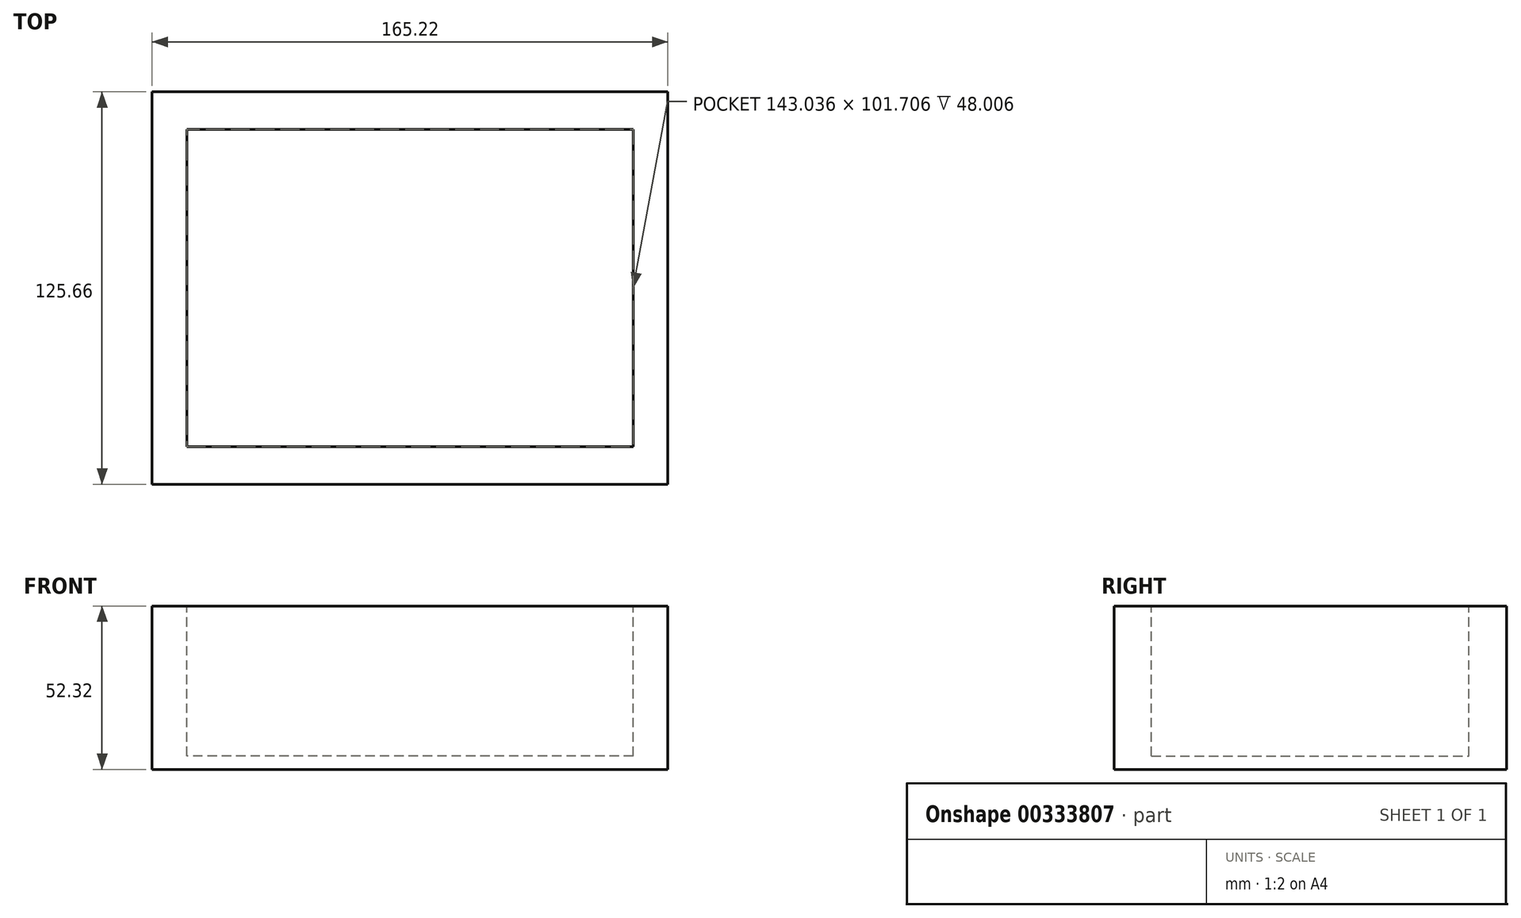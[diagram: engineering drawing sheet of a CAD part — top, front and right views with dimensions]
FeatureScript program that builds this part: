
annotation { "Feature Type Name" : "Feature", "Feature Type Description" : "" }
export const myFeature = defineFeature(function(context is Context, id is Id, definition is map)
    precondition{}
    {
        {
            var Q0;
            Q0=qCreatedBy(makeId("Top.planeOp"),FACE);
            var sketch = newSketch(context, id + "F0", { "sketchPlane" : qUnion([Q0])});
            skLineSegment(sketch, "E0.bottom", {"start": v(82.61, -62.83) * mm, "end": v(-82.61, -62.83) * mm});
            skLineSegment(sketch, "E0.top", {"start": v(82.61, 62.83) * mm, "end": v(-82.61, 62.83) * mm});
            skLineSegment(sketch, "E0.left", {"start": v(82.61, -62.83) * mm, "end": v(82.61, 62.83) * mm});
            skLineSegment(sketch, "E0.right", {"start": v(-82.61, -62.83) * mm, "end": v(-82.61, 62.83) * mm});
            skPoint(sketch, "E0.middle", {"position": v(0, 0) * mm});
            skSolve(sketch);
        }
        {
            var Q0;
            Q0 = qSketchRegion(id + "F0", true);
            extrude(context, id + "F1", {"entities" : qUnion([Q0]), "depth" : 52.32 * mm});
        }
        {
            var Q0;
            Q0=makeQuery(id+"F1.opExtrude","CAP_FACE",FACE,{"disambiguationData":[OSD([sQuery(id+"F0.wireOp",EDGE,"E0.bottom"),sQuery(id+"F0.wireOp",EDGE,"E0.top"),sQuery(id+"F0.wireOp",EDGE,"E0.left"),sQuery(id+"F0.wireOp",EDGE,"E0.right")])],"isStart":false});
            var sketch = newSketch(context, id + "F2", { "sketchPlane" : qUnion([Q0])});
            skLineSegment(sketch, "E1.bottom", {"start": v(71.52, -50.85) * mm, "end": v(-71.52, -50.85) * mm});
            skLineSegment(sketch, "E1.top", {"start": v(71.52, 50.85) * mm, "end": v(-71.52, 50.85) * mm});
            skLineSegment(sketch, "E1.left", {"start": v(71.52, -50.85) * mm, "end": v(71.52, 50.85) * mm});
            skLineSegment(sketch, "E1.right", {"start": v(-71.52, -50.85) * mm, "end": v(-71.52, 50.85) * mm});
            skPoint(sketch, "E1.middle", {"position": v(0, 0) * mm});
            skSolve(sketch);
        }
        {
            var Q0;
            Q0=makeQuery(id+"F2.imprint","IMPRINT",FACE,{"disambiguationData":[TD([[makeQuery(id+"F2.imprint","IMPRINT",EDGE,{"derivedFrom":sQuery(id+"F2.wireOp",EDGE,"E1.bottom")}),-1.0]])]});
            extrude(context, id + "F3", {"entities" : qUnion([Q0]), "operationType" : NewBodyOperationType.REMOVE, "oppositeDirection" : true, "depth" : 48 * mm});
        }
    });
